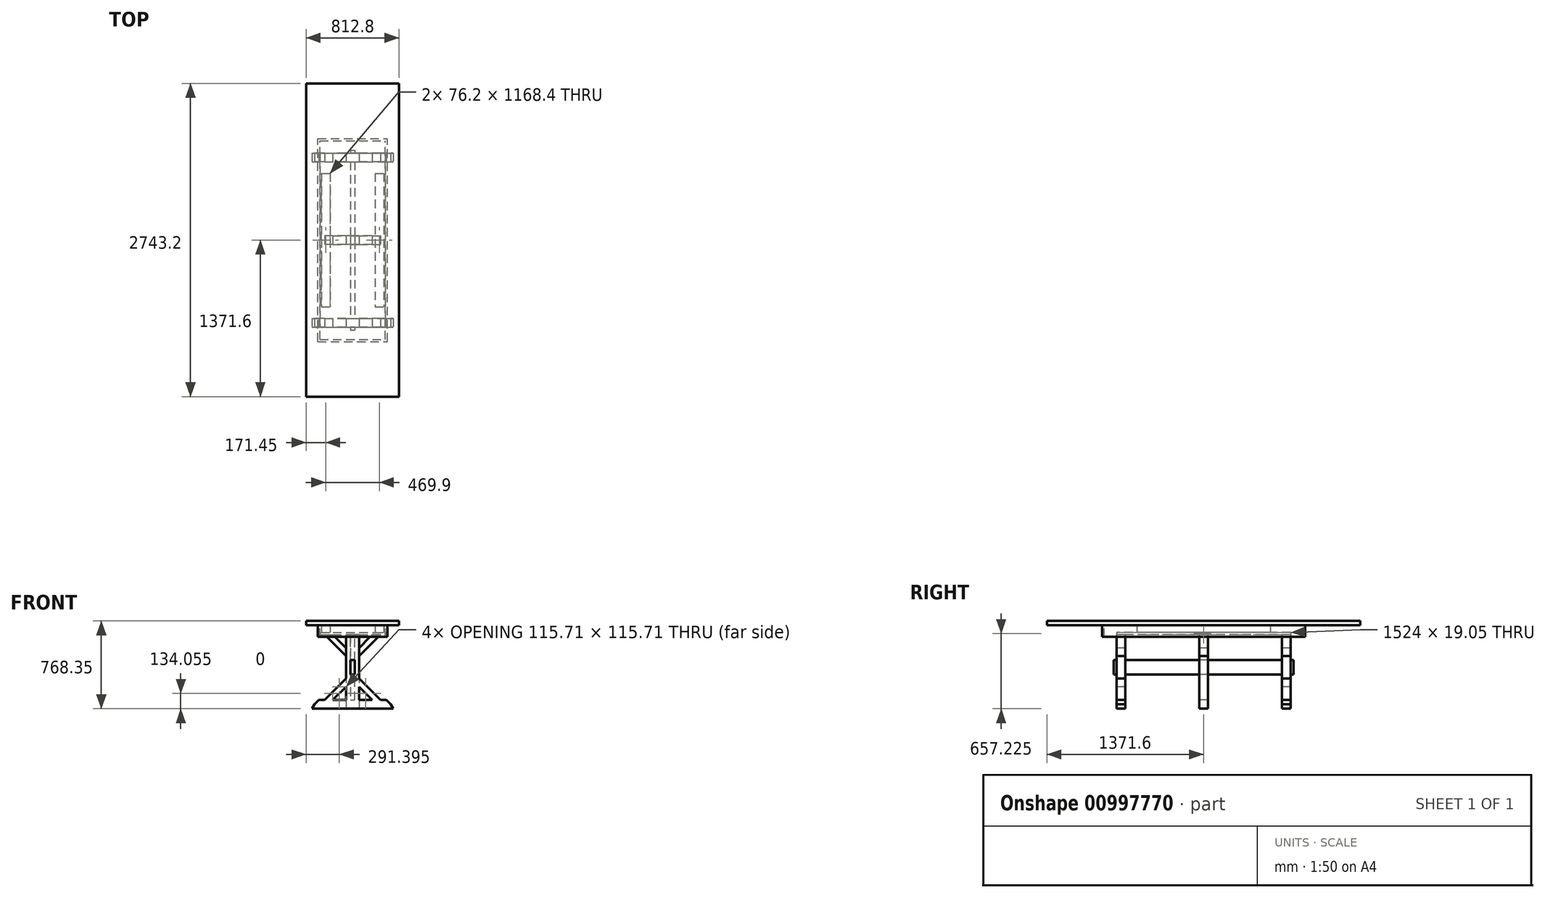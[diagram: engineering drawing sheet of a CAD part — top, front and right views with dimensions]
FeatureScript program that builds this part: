
annotation { "Feature Type Name" : "Feature", "Feature Type Description" : "" }
export const myFeature = defineFeature(function(context is Context, id is Id, definition is map)
    precondition{}
    {
        {
            var Q0;
            Q0=qCreatedBy(makeId("Front.planeOp"),FACE);
            var sketch = newSketch(context, id + "F0", { "sketchPlane" : qUnion([Q0])});
            skLineSegment(sketch, "E0", {"start": v(0, 76.2) * mm, "end": v(-295.5, 76.2) * mm});
            skLineSegment(sketch, "E1", {"start": v(-295.5, 76.2) * mm, "end": v(-333.6, 38.1) * mm});
            skLineSegment(sketch, "E2", {"start": v(0, 0) * mm, "end": v(0, 762) * mm, "construction": true});
            skLineSegment(sketch, "E3", {"start": v(-333.6, 38.1) * mm, "end": v(0, 38.1) * mm});
            skLineSegment(sketch, "E4", {"start": v(0, 76.2) * mm, "end": v(-19.05, 76.2) * mm});
            skLineSegment(sketch, "E5", {"start": v(-19.05, 76.2) * mm, "end": v(-19.05, 298.45) * mm});
            skLineSegment(sketch, "E6", {"start": v(-19.05, 298.45) * mm, "end": v(0, 298.45) * mm});
            skLineSegment(sketch, "E7", {"start": v(-19.05, 76.2) * mm, "end": v(-57.15, 76.2) * mm});
            skLineSegment(sketch, "E8", {"start": v(-57.15, 76.2) * mm, "end": v(-57.15, 647.7) * mm});
            skLineSegment(sketch, "E9", {"start": v(-57.15, 647.7) * mm, "end": v(-19.05, 647.7) * mm});
            skLineSegment(sketch, "E10", {"start": v(-19.05, 647.7) * mm, "end": v(-19.05, 76.2) * mm});
            skLineSegment(sketch, "E11", {"start": v(-355.6, 0) * mm, "end": v(0, 0) * mm});
            skLineSegment(sketch, "E12", {"start": v(0, 762) * mm, "end": v(-406.4, 762) * mm});
            skLineSegment(sketch, "E13", {"start": v(-406.4, 762) * mm, "end": v(-406.4, 723.9) * mm});
            skLineSegment(sketch, "E14", {"start": v(-406.4, 723.9) * mm, "end": v(0, 723.9) * mm});
            skLineSegment(sketch, "E15.bottom", {"start": v(-266.7, 723.9) * mm, "end": v(-200.03, 723.9) * mm, "construction": true});
            skLineSegment(sketch, "E15.top", {"start": v(-266.7, 666.75) * mm, "end": v(-200.03, 666.75) * mm, "construction": true});
            skLineSegment(sketch, "E15.left", {"start": v(-266.7, 723.9) * mm, "end": v(-266.7, 666.75) * mm, "construction": true});
            skLineSegment(sketch, "E15.right", {"start": v(-200.03, 723.9) * mm, "end": v(-200.03, 666.75) * mm, "construction": true});
            skLineSegment(sketch, "E16.bottom", {"start": v(-285.75, 666.75) * mm, "end": v(0, 666.75) * mm});
            skLineSegment(sketch, "E16.top", {"start": v(-285.75, 647.7) * mm, "end": v(0, 647.7) * mm});
            skLineSegment(sketch, "E16.left", {"start": v(-285.75, 666.75) * mm, "end": v(-285.75, 647.7) * mm});
            skLineSegment(sketch, "E17.bottom", {"start": v(-304.8, 723.9) * mm, "end": v(-285.75, 723.9) * mm});
            skLineSegment(sketch, "E17.top", {"start": v(-304.8, 622.3) * mm, "end": v(-285.75, 622.3) * mm});
            skLineSegment(sketch, "E17.left", {"start": v(-304.8, 723.9) * mm, "end": v(-304.8, 622.3) * mm});
            skLineSegment(sketch, "E17.right", {"start": v(-285.75, 723.9) * mm, "end": v(-285.75, 622.3) * mm});
            skLineSegment(sketch, "E18", {"start": v(-355.6, 0) * mm, "end": v(-333.6, 38.1) * mm});
            skLineSegment(sketch, "E19", {"start": v(-19.05, 647.7) * mm, "end": v(-19.05, 425.45) * mm});
            skLineSegment(sketch, "E20", {"start": v(-19.05, 425.45) * mm, "end": v(0, 425.45) * mm});
            skPoint(sketch, "E21", {"position": v(-19.05, 361.95) * mm});
            skLineSegment(sketch, "E22.MirrorCS", {"start": v(355.6, 0) * mm, "end": v(0, 0) * mm});
            skLineSegment(sketch, "E23.MirrorCS", {"start": v(333.6, 38.1) * mm, "end": v(0, 38.1) * mm});
            skLineSegment(sketch, "E24.MirrorCS", {"start": v(355.6, 0) * mm, "end": v(333.6, 38.1) * mm});
            skLineSegment(sketch, "E25.MirrorCS", {"start": v(295.5, 76.2) * mm, "end": v(333.6, 38.1) * mm});
            skLineSegment(sketch, "E26.MirrorCS", {"start": v(0, 76.2) * mm, "end": v(295.5, 76.2) * mm});
            skLineSegment(sketch, "E27.MirrorCS", {"start": v(57.15, 76.2) * mm, "end": v(57.15, 647.7) * mm});
            skLineSegment(sketch, "E28.MirrorCS", {"start": v(19.05, 647.7) * mm, "end": v(19.05, 76.2) * mm});
            skLineSegment(sketch, "E29.MirrorCS", {"start": v(19.05, 76.2) * mm, "end": v(57.15, 76.2) * mm});
            skLineSegment(sketch, "E30.MirrorCS", {"start": v(0, 762) * mm, "end": v(406.4, 762) * mm});
            skLineSegment(sketch, "E31.MirrorCS", {"start": v(406.4, 762) * mm, "end": v(406.4, 723.9) * mm});
            skLineSegment(sketch, "E32.MirrorCS", {"start": v(406.4, 723.9) * mm, "end": v(0, 723.9) * mm});
            skLineSegment(sketch, "E33.MirrorCS", {"start": v(285.75, 723.9) * mm, "end": v(285.75, 622.3) * mm});
            skLineSegment(sketch, "E34.MirrorCS", {"start": v(304.8, 723.9) * mm, "end": v(304.8, 622.3) * mm});
            skLineSegment(sketch, "E35.MirrorCS", {"start": v(304.8, 622.3) * mm, "end": v(285.75, 622.3) * mm});
            skLineSegment(sketch, "E36.MirrorCS", {"start": v(285.75, 647.7) * mm, "end": v(0, 647.7) * mm});
            skLineSegment(sketch, "E37.MirrorCS", {"start": v(266.7, 666.75) * mm, "end": v(200.03, 666.75) * mm, "construction": true});
            skLineSegment(sketch, "E38.MirrorCS", {"start": v(266.7, 723.9) * mm, "end": v(266.7, 666.75) * mm, "construction": true});
            skLineSegment(sketch, "E39.MirrorCS", {"start": v(200.03, 723.9) * mm, "end": v(200.03, 666.75) * mm, "construction": true});
            skLineSegment(sketch, "E40.MirrorCS", {"start": v(266.7, 723.9) * mm, "end": v(200.03, 723.9) * mm, "construction": true});
            skLineSegment(sketch, "E41.MirrorCS", {"start": v(285.75, 666.75) * mm, "end": v(0, 666.75) * mm});
            skLineSegment(sketch, "E42.MirrorCS", {"start": v(19.05, 425.45) * mm, "end": v(0, 425.45) * mm});
            skLineSegment(sketch, "E43.MirrorCS", {"start": v(19.05, 298.45) * mm, "end": v(0, 298.45) * mm});
            skLineSegment(sketch, "E44", {"start": v(57.15, 191.91) * mm, "end": v(172.86, 76.2) * mm});
            skLineSegment(sketch, "E45", {"start": v(172.86, 76.2) * mm, "end": v(244.7, 76.2) * mm});
            skLineSegment(sketch, "E46", {"start": v(244.7, 76.2) * mm, "end": v(57.15, 263.75) * mm});
            skLineSegment(sketch, "E47", {"start": v(57.15, 263.75) * mm, "end": v(57.15, 191.91) * mm});
            skLineSegment(sketch, "E48", {"start": v(-19.05, 361.95) * mm, "end": v(417.93, 361.95) * mm, "construction": true});
            skLineSegment(sketch, "E49.MirrorCS", {"start": v(244.7, 647.7) * mm, "end": v(57.15, 460.15) * mm});
            skLineSegment(sketch, "E50.MirrorCS", {"start": v(57.15, 531.99) * mm, "end": v(172.86, 647.7) * mm});
            skLineSegment(sketch, "E51.MirrorCS", {"start": v(-244.7, 76.2) * mm, "end": v(-57.15, 263.75) * mm});
            skLineSegment(sketch, "E52.MirrorCS", {"start": v(-57.15, 191.91) * mm, "end": v(-172.86, 76.2) * mm});
            skLineSegment(sketch, "E53.MirrorCS", {"start": v(-244.7, 647.7) * mm, "end": v(-57.15, 460.15) * mm});
            skLineSegment(sketch, "E54.MirrorCS", {"start": v(-57.15, 531.99) * mm, "end": v(-172.86, 647.7) * mm});
            skSolve(sketch);
        }
        {
            var Q0;
            Q0=makeQuery(id+"F0.imprint","IMPRINT",FACE,{"disambiguationData":[TD([[makeQuery(id+"F0.imprint","IMPRINT",EDGE,{"derivedFrom":sQuery(id+"F0.wireOp",EDGE,"E3")}),-1.0]])]});
            var Q1;
            {var subQ4=sQuery(id+"F0.wireOp",EDGE,"E1");Q1=makeQuery(id+"F0.imprint","IMPRINT",FACE,{"disambiguationData":[TD([[makeQuery(id+"F0.imprint","IMPRINT",EDGE,{"derivedFrom":subQ4}),1.0]])]});}
            extrude(context, id + "F1", {"entities" : qUnion([Q0, Q1]), "oppositeDirection" : true, "depth" : 76.2 * mm, "offsetDistance" : 25.4 * mm});
        }
        {
            var Q0;
            {var subQ0=sQuery(id+"F0.wireOp",EDGE,"E27.MirrorCS");var subQ4=sQuery(id+"F0.wireOp",EDGE,"E26.MirrorCS");var subQ5=makeQuery(id+"F0.imprint","INTERSECT",VERTEX,{"derivedFrom":[subQ4,subQ0]});Q0=makeQuery(id+"F0.imprint","IMPRINT",FACE,{"disambiguationData":[TD([[makeQuery(id+"F0.imprint","IMPRINT",EDGE,{"disambiguationData":[TD([[subQ5,1.0]])],"derivedFrom":subQ4}),1.0]])]});}
            var Q1;
            {var subQ6=sQuery(id+"F0.wireOp",EDGE,"E5");Q1=makeQuery(id+"F0.imprint","IMPRINT",FACE,{"disambiguationData":[TD([[makeQuery(id+"F0.imprint","IMPRINT",EDGE,{"derivedFrom":subQ6}),1.0]])]});}
            extrude(context, id + "F2", {"entities" : qUnion([Q0, Q1]), "operationType" : NewBodyOperationType.ADD, "oppositeDirection" : true, "depth" : 76.2 * mm, "offsetDistance" : 25.4 * mm});
        }
        {
            var Q0;
            {var subQ0=sQuery(id+"F0.wireOp",EDGE,"E51.MirrorCS");Q0=makeQuery(id+"F0.imprint","IMPRINT",FACE,{"disambiguationData":[TD([[makeQuery(id+"F0.imprint","IMPRINT",EDGE,{"derivedFrom":subQ0}),-1.0]])]});}
            var Q1;
            {var subQ0=sQuery(id+"F0.wireOp",EDGE,"E44");Q1=makeQuery(id+"F0.imprint","IMPRINT",FACE,{"disambiguationData":[TD([[makeQuery(id+"F0.imprint","IMPRINT",EDGE,{"derivedFrom":subQ0}),1.0]])]});}
            extrude(context, id + "F3", {"entities" : qUnion([Q0, Q1]), "operationType" : NewBodyOperationType.ADD, "oppositeDirection" : true, "depth" : 76.2 * mm, "offsetDistance" : 25.4 * mm});
        }
        {
            var Q0;
            {var subQ5=sQuery(id+"F0.wireOp",EDGE,"E5");Q0=makeQuery(id+"F0.imprint","IMPRINT",FACE,{"disambiguationData":[TD([[makeQuery(id+"F0.imprint","IMPRINT",EDGE,{"derivedFrom":subQ5}),-1.0]])]});}
            var Q1;
            {var subQ0=sQuery(id+"F0.wireOp",EDGE,"E20");Q1=makeQuery(id+"F0.imprint","IMPRINT",FACE,{"disambiguationData":[TD([[makeQuery(id+"F0.imprint","IMPRINT",EDGE,{"derivedFrom":subQ0}),1.0]])]});}
            extrude(context, id + "F4", {"entities" : qUnion([Q0, Q1]), "oppositeDirection" : true, "depth" : 76.2 * mm, "offsetDistance" : 25.4 * mm});
        }
        {
            var Q0;
            {var subQ2=sQuery(id+"F0.wireOp",EDGE,"E53.MirrorCS");Q0=makeQuery(id+"F0.imprint","IMPRINT",FACE,{"disambiguationData":[TD([[makeQuery(id+"F0.imprint","IMPRINT",EDGE,{"derivedFrom":subQ2}),1.0]])]});}
            var Q1;
            {var subQ2=sQuery(id+"F0.wireOp",EDGE,"E49.MirrorCS");Q1=makeQuery(id+"F0.imprint","IMPRINT",FACE,{"disambiguationData":[TD([[makeQuery(id+"F0.imprint","IMPRINT",EDGE,{"derivedFrom":subQ2}),-1.0]])]});}
            extrude(context, id + "F5", {"entities" : qUnion([Q0, Q1]), "oppositeDirection" : true, "depth" : 76.2 * mm, "offsetDistance" : 25.4 * mm});
        }
        {
            var Q0;
            {var subQ0=sQuery(id+"F0.wireOp",EDGE,"E27.MirrorCS");var subQ1=sQuery(id+"F0.wireOp",EDGE,"E26.MirrorCS");var subQ2=sQuery(id+"F0.wireOp",EDGE,"E8");var subQ3=sQuery(id+"F0.wireOp",EDGE,"E0");Q0=makeQuery(id+"F3.boolean.opBoolean","MERGE",FACE,{"derivedFrom":[makeQuery(id+"F2.boolean.opBoolean","MERGE",FACE,{"derivedFrom":[makeQuery(id+"F1.opExtrude","CAP_FACE",FACE,{"disambiguationData":[OSD([subQ3,sQuery(id+"F0.wireOp",EDGE,"E1"),sQuery(id+"F0.wireOp",EDGE,"E11"),sQuery(id+"F0.wireOp",EDGE,"E18"),sQuery(id+"F0.wireOp",EDGE,"E22.MirrorCS"),sQuery(id+"F0.wireOp",EDGE,"E24.MirrorCS"),sQuery(id+"F0.wireOp",EDGE,"E25.MirrorCS"),subQ1])],"isStart":false}),makeQuery(id+"F2.opExtrude","CAP_FACE",FACE,{"disambiguationData":[OSD([subQ3,sQuery(id+"F0.wireOp",EDGE,"E5"),subQ2,sQuery(id+"F0.wireOp",EDGE,"E9"),sQuery(id+"F0.wireOp",EDGE,"E10")])],"isStart":false}),makeQuery(id+"F2.opExtrude","CAP_FACE",FACE,{"disambiguationData":[OSD([subQ1,subQ0,sQuery(id+"F0.wireOp",EDGE,"E28.MirrorCS"),sQuery(id+"F0.wireOp",EDGE,"E36.MirrorCS")])],"isStart":false})]}),makeQuery(id+"F3.opExtrude","CAP_FACE",FACE,{"disambiguationData":[OSD([subQ3,subQ2,sQuery(id+"F0.wireOp",EDGE,"E51.MirrorCS"),sQuery(id+"F0.wireOp",EDGE,"E52.MirrorCS")])],"isStart":false}),makeQuery(id+"F3.opExtrude","CAP_FACE",FACE,{"disambiguationData":[OSD([subQ1,subQ0,sQuery(id+"F0.wireOp",EDGE,"E44"),sQuery(id+"F0.wireOp",EDGE,"E46")])],"isStart":false})]});}
            var Q1;
            Q1=makeQuery(id+"F5.opExtrude","CAP_FACE",FACE,{"disambiguationData":[OSD([sQuery(id+"F0.wireOp",EDGE,"E27.MirrorCS"),sQuery(id+"F0.wireOp",EDGE,"E36.MirrorCS"),sQuery(id+"F0.wireOp",EDGE,"E49.MirrorCS"),sQuery(id+"F0.wireOp",EDGE,"E50.MirrorCS")])],"isStart":false});
            var Q2;
            Q2=makeQuery(id+"F5.opExtrude","CAP_FACE",FACE,{"disambiguationData":[OSD([sQuery(id+"F0.wireOp",EDGE,"E8"),sQuery(id+"F0.wireOp",EDGE,"E16.top"),sQuery(id+"F0.wireOp",EDGE,"E53.MirrorCS"),sQuery(id+"F0.wireOp",EDGE,"E54.MirrorCS")])],"isStart":false});
            var Q3;
            Q3=makeQuery(id+"F4.opExtrude","CAP_FACE",FACE,{"disambiguationData":[OSD([sQuery(id+"F0.wireOp",EDGE,"E10"),sQuery(id+"F0.wireOp",EDGE,"E16.top"),sQuery(id+"F0.wireOp",EDGE,"E20"),sQuery(id+"F0.wireOp",EDGE,"E28.MirrorCS"),sQuery(id+"F0.wireOp",EDGE,"E36.MirrorCS"),sQuery(id+"F0.wireOp",EDGE,"E42.MirrorCS")])],"isStart":false});
            var Q4;
            Q4=makeQuery(id+"F4.opExtrude","CAP_FACE",FACE,{"disambiguationData":[OSD([sQuery(id+"F0.wireOp",EDGE,"E0"),sQuery(id+"F0.wireOp",EDGE,"E5"),sQuery(id+"F0.wireOp",EDGE,"E6"),sQuery(id+"F0.wireOp",EDGE,"E26.MirrorCS"),sQuery(id+"F0.wireOp",EDGE,"E28.MirrorCS"),sQuery(id+"F0.wireOp",EDGE,"E43.MirrorCS")])],"isStart":false});
            extrude(context, id + "F6", {"entities" : qUnion([Q0, Q1, Q2, Q3, Q4]), "depth" : 1447.8 * mm, "offsetDistance" : 25.4 * mm});
        }
        {
            var Q0;
            Q0=qCreatedBy(makeId("Right.planeOp"),FACE);
            var sketch = newSketch(context, id + "F7", { "sketchPlane" : qUnion([Q0])});
            skLineSegment(sketch, "E55.bottom", {"start": v(76.2, -1.7) * mm, "end": v(723.9, -1.7) * mm});
            skLineSegment(sketch, "E55.top", {"start": v(76.2, 696.31) * mm, "end": v(723.9, 696.31) * mm});
            skLineSegment(sketch, "E55.left", {"start": v(76.2, -1.7) * mm, "end": v(76.2, 696.31) * mm});
            skLineSegment(sketch, "E55.right", {"start": v(1447.8, -1.7) * mm, "end": v(1447.8, 696.31) * mm});
            skLineSegment(sketch, "E56.left", {"start": v(800.1, 696.31) * mm, "end": v(800.1, -1.7) * mm});
            skLineSegment(sketch, "E56.right", {"start": v(723.9, 696.31) * mm, "end": v(723.9, -1.7) * mm});
            skPoint(sketch, "E57", {"position": v(762, 696.31) * mm});
            skLineSegment(sketch, "E58.trimOffspring", {"start": v(800.1, -1.7) * mm, "end": v(1447.8, -1.7) * mm});
            skLineSegment(sketch, "E59.trimOffspring", {"start": v(800.1, 696.31) * mm, "end": v(1447.8, 696.31) * mm});
            skSolve(sketch);
        }
        {
            var Q0;
            Q0=qSketchRegion(id+"F7",true);
            extrude(context, id + "F8", {"entities" : qUnion([Q0]), "operationType" : NewBodyOperationType.REMOVE, "endBound" : BoundingType.SYMMETRIC, "oppositeDirection" : true, "depth" : 1016 * mm, "offsetDistance" : 25.4 * mm});
        }
        {
            var Q0;
            {var subQ5=sQuery(id+"F0.wireOp",EDGE,"E6");Q0=makeQuery(id+"F0.imprint","IMPRINT",FACE,{"disambiguationData":[TD([[makeQuery(id+"F0.imprint","IMPRINT",EDGE,{"derivedFrom":subQ5}),1.0]])]});}
            extrude(context, id + "F9", {"entities" : qUnion([Q0]), "oppositeDirection" : true, "depth" : 1524 * mm, "offsetDistance" : 25.4 * mm});
        }
        {
            var Q0;
            {var subQ5=sQuery(id+"F0.wireOp",EDGE,"E6");Q0=makeQuery(id+"F0.imprint","IMPRINT",FACE,{"disambiguationData":[TD([[makeQuery(id+"F0.imprint","IMPRINT",EDGE,{"derivedFrom":subQ5}),1.0]])]});}
            extrude(context, id + "F10", {"entities" : qUnion([Q0]), "operationType" : NewBodyOperationType.ADD, "depth" : 25.4 * mm, "offsetDistance" : 25.4 * mm});
        }
        {
            var Q0;
            Q0=makeQuery(id+"F9.opExtrude","CAP_FACE",FACE,{"disambiguationData":[OSD([sQuery(id+"F0.wireOp",EDGE,"E6"),sQuery(id+"F0.wireOp",EDGE,"E10"),sQuery(id+"F0.wireOp",EDGE,"E20"),sQuery(id+"F0.wireOp",EDGE,"E28.MirrorCS"),sQuery(id+"F0.wireOp",EDGE,"E42.MirrorCS"),sQuery(id+"F0.wireOp",EDGE,"E43.MirrorCS")])],"isStart":false});
            extrude(context, id + "F11", {"entities" : qUnion([Q0]), "operationType" : NewBodyOperationType.ADD, "depth" : 25.4 * mm, "offsetDistance" : 25.4 * mm});
        }
        {
            var Q0;
            {var subQ4=sQuery(id+"F0.wireOp",EDGE,"E36.MirrorCS");var subQ5=makeQuery(id+"F6.opExtrude","SWEPT_FACE",FACE,{"disambiguationData":[OSD([subQ4]),TDD([makeQuery(id+"F5.opExtrude","CAP_EDGE",EDGE,{"disambiguationData":[OSD([subQ4])],"isStart":false})])]});Q0=qUnion([makeQuery(id+"F8.boolean.opBoolean","SPLIT",FACE,{"disambiguationData":[TD([makeQuery(id+"F8.opExtrude","SWEPT_FACE",FACE,{"disambiguationData":[OSD([sQuery(id+"F7.wireOp",EDGE,"E55.right")])]})])],"derivedFrom":subQ5}),makeQuery(id+"F8.boolean.opBoolean","SPLIT",FACE,{"disambiguationData":[TD([makeQuery(id+"F8.opExtrude","SWEPT_FACE",FACE,{"disambiguationData":[OSD([sQuery(id+"F7.wireOp",EDGE,"E56.left")])]})])],"derivedFrom":subQ5})]);}
            var sketch = newSketch(context, id + "F12", { "sketchPlane" : qUnion([Q0])});
            skLineSegment(sketch, "E60.bottom", {"start": v(-285.75, 1524) * mm, "end": v(285.75, 1524) * mm});
            skLineSegment(sketch, "E60.top", {"start": v(-285.75, 0) * mm, "end": v(285.75, 0) * mm});
            skLineSegment(sketch, "E60.left", {"start": v(-285.75, 1524) * mm, "end": v(-285.75, 0) * mm});
            skLineSegment(sketch, "E60.right", {"start": v(285.75, 1524) * mm, "end": v(285.75, 0) * mm});
            skSolve(sketch);
        }
        {
            var Q0;
            Q0=qSketchRegion(id+"F12",true);
            extrude(context, id + "F13", {"entities" : qUnion([Q0]), "depth" : 19.05 * mm, "offsetDistance" : 25.4 * mm});
        }
        {
            var Q0;
            Q0=makeQuery(id+"F13.opExtrude","CAP_FACE",FACE,{"disambiguationData":[OSD([sQuery(id+"F12.wireOp",EDGE,"E60.bottom"),sQuery(id+"F12.wireOp",EDGE,"E60.top"),sQuery(id+"F12.wireOp",EDGE,"E60.left"),sQuery(id+"F12.wireOp",EDGE,"E60.right")])],"isStart":false});
            var sketch = newSketch(context, id + "F14", { "sketchPlane" : qUnion([Q0])});
            skLineSegment(sketch, "E61", {"start": v(-273.05, 762) * mm, "end": v(273.05, 762) * mm, "construction": true});
            skLineSegment(sketch, "E62.bottom", {"start": v(-273.05, 1346.2) * mm, "end": v(-196.85, 1346.2) * mm});
            skLineSegment(sketch, "E62.top", {"start": v(-273.05, 177.8) * mm, "end": v(-196.85, 177.8) * mm});
            skLineSegment(sketch, "E62.left", {"start": v(-273.05, 1346.2) * mm, "end": v(-273.05, 177.8) * mm});
            skLineSegment(sketch, "E62.right", {"start": v(-196.85, 1346.2) * mm, "end": v(-196.85, 177.8) * mm});
            skLineSegment(sketch, "E63.bottom", {"start": v(196.85, 1346.2) * mm, "end": v(273.05, 1346.2) * mm});
            skLineSegment(sketch, "E63.top", {"start": v(196.85, 177.8) * mm, "end": v(273.05, 177.8) * mm});
            skLineSegment(sketch, "E63.left", {"start": v(196.85, 1346.2) * mm, "end": v(196.85, 177.8) * mm});
            skLineSegment(sketch, "E63.right", {"start": v(273.05, 1346.2) * mm, "end": v(273.05, 177.8) * mm});
            skSolve(sketch);
        }
        {
            var Q0;
            Q0=makeQuery(id+"F14.imprint","IMPRINT",FACE,{"disambiguationData":[TD([[makeQuery(id+"F14.imprint","IMPRINT",EDGE,{"derivedFrom":sQuery(id+"F14.wireOp",EDGE,"E62.bottom")}),-1.0]])]});
            var Q1;
            Q1=makeQuery(id+"F14.imprint","IMPRINT",FACE,{"disambiguationData":[TD([[makeQuery(id+"F14.imprint","IMPRINT",EDGE,{"derivedFrom":sQuery(id+"F14.wireOp",EDGE,"E63.bottom")}),-1.0]])]});
            extrude(context, id + "F15", {"entities" : qUnion([Q0, Q1]), "operationType" : NewBodyOperationType.ADD, "depth" : 63.5 * mm, "offsetDistance" : 25.4 * mm});
        }
        {
            var Q0;
            Q0=makeQuery(id+"F15.opExtrude","CAP_FACE",FACE,{"disambiguationData":[OSD([sQuery(id+"F14.wireOp",EDGE,"E62.bottom"),sQuery(id+"F14.wireOp",EDGE,"E62.top"),sQuery(id+"F14.wireOp",EDGE,"E62.left"),sQuery(id+"F14.wireOp",EDGE,"E62.right")])],"isStart":false});
            var sketch = newSketch(context, id + "F16", { "sketchPlane" : qUnion([Q0])});
            skLineSegment(sketch, "E64.bottom", {"start": v(-406.4, 2133.6) * mm, "end": v(406.4, 2133.6) * mm});
            skLineSegment(sketch, "E64.top", {"start": v(-406.4, -609.6) * mm, "end": v(406.4, -609.6) * mm});
            skLineSegment(sketch, "E64.left", {"start": v(-406.4, 2133.6) * mm, "end": v(-406.4, 381) * mm});
            skLineSegment(sketch, "E64.right", {"start": v(406.4, 2133.6) * mm, "end": v(406.4, 381) * mm});
            skLineSegment(sketch, "E65", {"start": v(0, 0) * mm, "end": v(0, -609.6) * mm, "construction": true});
            skLineSegment(sketch, "E66.trimOffspring", {"start": v(-406.4, 381) * mm, "end": v(-406.4, -609.6) * mm});
            skLineSegment(sketch, "E67.trimOffspring", {"start": v(406.4, 381) * mm, "end": v(406.4, -609.6) * mm});
            skSolve(sketch);
        }
        {
            var Q0;
            Q0=qSketchRegion(id+"F16",true);
            extrude(context, id + "F17", {"entities" : qUnion([Q0]), "operationType" : NewBodyOperationType.ADD, "depth" : 38.1 * mm, "offsetDistance" : 25.4 * mm});
        }
        {
            var Q0;
            Q0=makeQuery(id+"F17.opExtrude","CAP_FACE",FACE,{"disambiguationData":[OSD([sQuery(id+"F16.wireOp",EDGE,"E64.bottom"),sQuery(id+"F16.wireOp",EDGE,"E64.top"),sQuery(id+"F16.wireOp",EDGE,"E64.left"),sQuery(id+"F16.wireOp",EDGE,"E64.right")])],"isStart":true});
            var sketch = newSketch(context, id + "F18", { "sketchPlane" : qUnion([Q0])});
            skLineSegment(sketch, "E68.bottom", {"start": v(-304.8, 127) * mm, "end": v(304.8, 127) * mm});
            skLineSegment(sketch, "E68.top", {"start": v(-304.8, -1651) * mm, "end": v(304.8, -1651) * mm});
            skLineSegment(sketch, "E68.left", {"start": v(-304.8, 127) * mm, "end": v(-304.8, -1651) * mm});
            skLineSegment(sketch, "E68.right", {"start": v(304.8, 127) * mm, "end": v(304.8, -1651) * mm});
            skLineSegment(sketch, "E69.bottom", {"start": v(-285.75, 107.95) * mm, "end": v(285.75, 107.95) * mm});
            skLineSegment(sketch, "E69.top", {"start": v(-285.75, -1631.95) * mm, "end": v(273.05, -1631.95) * mm});
            skLineSegment(sketch, "E69.left", {"start": v(-285.75, 107.95) * mm, "end": v(-285.75, -1631.95) * mm});
            skLineSegment(sketch, "E69.right", {"start": v(285.75, 107.95) * mm, "end": v(285.75, -1631.95) * mm});
            skLineSegment(sketch, "E70", {"start": v(273.05, -1631.95) * mm, "end": v(285.75, -1631.95) * mm});
            skSolve(sketch);
        }
        {
            var Q0;
            {var subQ13=sQuery(id+"F18.wireOp",EDGE,"E68.bottom");Q0=makeQuery(id+"F18.imprint","IMPRINT",FACE,{"disambiguationData":[TD([[makeQuery(id+"F18.imprint","IMPRINT",EDGE,{"derivedFrom":subQ13}),-1.0]])]});}
            var Q1;
            {var subQ2=sQuery(id+"F18.wireOp",EDGE,"E68.top");Q1=makeQuery(id+"F18.imprint","IMPRINT",FACE,{"disambiguationData":[TD([[makeQuery(id+"F18.imprint","IMPRINT",EDGE,{"derivedFrom":subQ2}),1.0]])]});}
            extrude(context, id + "F19", {"entities" : qUnion([Q0, Q1]), "operationType" : NewBodyOperationType.ADD, "depth" : 101.6 * mm, "offsetDistance" : 25.4 * mm});
        }
        {
            var Q0;
            {var subQ13=sQuery(id+"F0.wireOp",EDGE,"E1");Q0=makeQuery(id+"F8.boolean.opBoolean","COPY",FACE,{"disambiguationData":[TD([makeQuery(id+"F6.opExtrude","SWEPT_FACE",FACE,{"disambiguationData":[OSD([subQ13])]})])],"derivedFrom":makeQuery(id+"F8.opExtrude","SWEPT_FACE",FACE,{"disambiguationData":[OSD([sQuery(id+"F7.wireOp",EDGE,"E56.left")])]})});}
            var sketch = newSketch(context, id + "F20", { "sketchPlane" : qUnion([Q0])});
            skLineSegment(sketch, "E71.bottom", {"start": v(57.15, 263.75) * mm, "end": v(510, 263.75) * mm});
            skLineSegment(sketch, "E71.top", {"start": v(57.15, -83.18) * mm, "end": v(510, -83.18) * mm});
            skLineSegment(sketch, "E71.left", {"start": v(57.15, 263.75) * mm, "end": v(57.15, -83.18) * mm});
            skLineSegment(sketch, "E71.right", {"start": v(510, 263.75) * mm, "end": v(510, -83.18) * mm});
            skLineSegment(sketch, "E72.bottom", {"start": v(-57.15, 263.75) * mm, "end": v(-399.16, 263.75) * mm});
            skLineSegment(sketch, "E72.top", {"start": v(-57.15, -37.53) * mm, "end": v(-399.16, -37.53) * mm});
            skLineSegment(sketch, "E72.left", {"start": v(-57.15, 263.75) * mm, "end": v(-57.15, -37.53) * mm});
            skLineSegment(sketch, "E72.right", {"start": v(-399.16, 263.75) * mm, "end": v(-399.16, -37.53) * mm});
            skSolve(sketch);
        }
        {
            var Q0;
            Q0=qSketchRegion(id+"F20",true);
            extrude(context, id + "F21", {"entities" : qUnion([Q0]), "operationType" : NewBodyOperationType.REMOVE, "oppositeDirection" : true, "depth" : 101.6 * mm, "offsetDistance" : 25.4 * mm});
        }
    });
